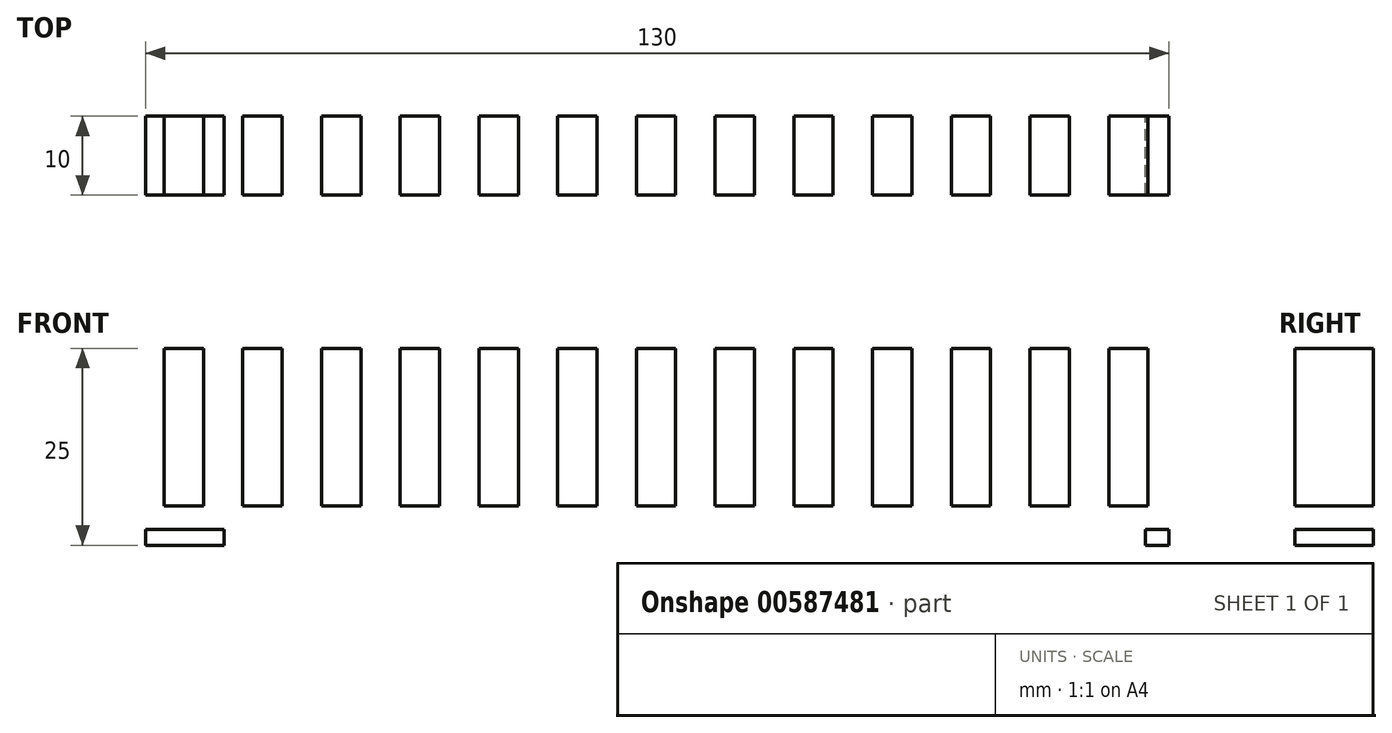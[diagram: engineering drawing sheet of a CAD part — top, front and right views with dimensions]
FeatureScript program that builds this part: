
annotation { "Feature Type Name" : "Feature", "Feature Type Description" : "" }
export const myFeature = defineFeature(function(context is Context, id is Id, definition is map)
    precondition{}
    {
        {
            var Q0;
            Q0=qCreatedBy(makeId("Front.planeOp"),FACE);
            var sketch = newSketch(context, id + "F0", { "sketchPlane" : qUnion([Q0])});
            skLineSegment(sketch, "E0.bottom", {"start": v(-65, 2.5) * mm, "end": v(65, 2.5) * mm});
            skLineSegment(sketch, "E0.top", {"start": v(-65, -2.5) * mm, "end": v(65, -2.5) * mm});
            skLineSegment(sketch, "E0.left", {"start": v(-65, 2.5) * mm, "end": v(-65, -2.5) * mm});
            skLineSegment(sketch, "E0.right", {"start": v(65, 2.5) * mm, "end": v(65, -2.5) * mm});
            skPoint(sketch, "E0.middle", {"position": v(0, 0) * mm});
            skLineSegment(sketch, "E1.bottom", {"start": v(-64.85, 2.5) * mm, "end": v(-59.85, 2.5) * mm});
            skLineSegment(sketch, "E1.top", {"start": v(-62.65, 22.5) * mm, "end": v(-57.65, 22.5) * mm});
            skLineSegment(sketch, "E1.left", {"start": v(-62.65, 2.5) * mm, "end": v(-62.65, 22.5) * mm});
            skLineSegment(sketch, "E1.right", {"start": v(-57.65, 2.5) * mm, "end": v(-57.65, 22.5) * mm});
            skLineSegment(sketch, "E2.1.0.0", {"start": v(-52.65, 22.5) * mm, "end": v(-47.65, 22.5) * mm});
            skLineSegment(sketch, "E2.1.0.1", {"start": v(-47.65, 2.5) * mm, "end": v(-47.65, 22.5) * mm});
            skLineSegment(sketch, "E2.1.0.2", {"start": v(-52.65, 2.5) * mm, "end": v(-52.65, 22.5) * mm});
            skLineSegment(sketch, "E2.2.0.0", {"start": v(-42.65, 22.5) * mm, "end": v(-37.65, 22.5) * mm});
            skLineSegment(sketch, "E2.2.0.1", {"start": v(-37.65, 2.5) * mm, "end": v(-37.65, 22.5) * mm});
            skLineSegment(sketch, "E2.2.0.2", {"start": v(-42.65, 2.5) * mm, "end": v(-42.65, 22.5) * mm});
            skLineSegment(sketch, "E2.3.0.0", {"start": v(-32.65, 22.5) * mm, "end": v(-27.65, 22.5) * mm});
            skLineSegment(sketch, "E2.3.0.1", {"start": v(-27.65, 2.5) * mm, "end": v(-27.65, 22.5) * mm});
            skLineSegment(sketch, "E2.3.0.2", {"start": v(-32.65, 2.5) * mm, "end": v(-32.65, 22.5) * mm});
            skLineSegment(sketch, "E2.4.0.0", {"start": v(-22.65, 22.5) * mm, "end": v(-17.65, 22.5) * mm});
            skLineSegment(sketch, "E2.4.0.1", {"start": v(-17.65, 2.5) * mm, "end": v(-17.65, 22.5) * mm});
            skLineSegment(sketch, "E2.4.0.2", {"start": v(-22.65, 2.5) * mm, "end": v(-22.65, 22.5) * mm});
            skLineSegment(sketch, "E2.5.0.0", {"start": v(-12.65, 22.5) * mm, "end": v(-7.65, 22.5) * mm});
            skLineSegment(sketch, "E2.5.0.1", {"start": v(-7.65, 2.5) * mm, "end": v(-7.65, 22.5) * mm});
            skLineSegment(sketch, "E2.5.0.2", {"start": v(-12.65, 2.5) * mm, "end": v(-12.65, 22.5) * mm});
            skLineSegment(sketch, "E2.6.0.0", {"start": v(-2.65, 22.5) * mm, "end": v(2.35, 22.5) * mm});
            skLineSegment(sketch, "E2.6.0.1", {"start": v(2.35, 2.5) * mm, "end": v(2.35, 22.5) * mm});
            skLineSegment(sketch, "E2.6.0.2", {"start": v(-2.65, 2.5) * mm, "end": v(-2.65, 22.5) * mm});
            skLineSegment(sketch, "E2.7.0.0", {"start": v(7.35, 22.5) * mm, "end": v(12.35, 22.5) * mm});
            skLineSegment(sketch, "E2.7.0.1", {"start": v(12.35, 2.5) * mm, "end": v(12.35, 22.5) * mm});
            skLineSegment(sketch, "E2.7.0.2", {"start": v(7.35, 2.5) * mm, "end": v(7.35, 22.5) * mm});
            skLineSegment(sketch, "E2.8.0.0", {"start": v(17.35, 22.5) * mm, "end": v(22.35, 22.5) * mm});
            skLineSegment(sketch, "E2.8.0.1", {"start": v(22.35, 2.5) * mm, "end": v(22.35, 22.5) * mm});
            skLineSegment(sketch, "E2.8.0.2", {"start": v(17.35, 2.5) * mm, "end": v(17.35, 22.5) * mm});
            skLineSegment(sketch, "E2.9.0.0", {"start": v(27.35, 22.5) * mm, "end": v(32.35, 22.5) * mm});
            skLineSegment(sketch, "E2.9.0.1", {"start": v(32.35, 2.5) * mm, "end": v(32.35, 22.5) * mm});
            skLineSegment(sketch, "E2.9.0.2", {"start": v(27.35, 2.5) * mm, "end": v(27.35, 22.5) * mm});
            skLineSegment(sketch, "E3.1.0.0", {"start": v(37.35, 2.5) * mm, "end": v(37.35, 22.5) * mm});
            skLineSegment(sketch, "E3.1.0.1", {"start": v(37.35, 22.5) * mm, "end": v(42.35, 22.5) * mm});
            skLineSegment(sketch, "E3.1.0.2", {"start": v(42.35, 2.5) * mm, "end": v(42.35, 22.5) * mm});
            skLineSegment(sketch, "E3.2.0.0", {"start": v(47.35, 2.5) * mm, "end": v(47.35, 22.5) * mm});
            skLineSegment(sketch, "E3.2.0.1", {"start": v(47.35, 22.5) * mm, "end": v(52.35, 22.5) * mm});
            skLineSegment(sketch, "E3.2.0.2", {"start": v(52.35, 2.5) * mm, "end": v(52.35, 22.5) * mm});
            skLineSegment(sketch, "E3.3.0.0", {"start": v(57.35, 2.5) * mm, "end": v(57.35, 22.5) * mm});
            skLineSegment(sketch, "E3.3.0.1", {"start": v(57.35, 22.5) * mm, "end": v(62.35, 22.5) * mm});
            skLineSegment(sketch, "E3.3.0.2", {"start": v(62.35, 2.5) * mm, "end": v(62.35, 22.5) * mm});
            skLineSegment(sketch, "E3.direction1", {"start": v(25.15, 2.5) * mm, "end": v(35.15, 2.5) * mm, "construction": true});
            skLineSegment(sketch, "E4.bottom", {"start": v(65, -0.5) * mm, "end": v(62, -0.5) * mm});
            skLineSegment(sketch, "E4.top", {"start": v(65, -2.5) * mm, "end": v(62, -2.5) * mm});
            skLineSegment(sketch, "E4.left", {"start": v(65, -0.5) * mm, "end": v(65, -2.5) * mm});
            skLineSegment(sketch, "E4.right", {"start": v(62, -0.5) * mm, "end": v(62, -2.5) * mm});
            skLineSegment(sketch, "E5.bottom", {"start": v(-65, -0.5) * mm, "end": v(-55, -0.5) * mm});
            skLineSegment(sketch, "E5.top", {"start": v(-65, -2.5) * mm, "end": v(-55, -2.5) * mm});
            skLineSegment(sketch, "E5.left", {"start": v(-65, -0.5) * mm, "end": v(-65, -2.5) * mm});
            skLineSegment(sketch, "E5.right", {"start": v(-55, -0.5) * mm, "end": v(-55, -2.5) * mm});
            skSolve(sketch);
        }
        {
            var Q0;
            {var subQ0=sQuery(id+"F0.wireOp",EDGE,"E3.3.0.0");Q0=makeQuery(id+"F0.imprint","IMPRINT",FACE,{"disambiguationData":[TD([[makeQuery(id+"F0.imprint","IMPRINT",EDGE,{"derivedFrom":subQ0}),-1.0]])]});}
            var Q1;
            {var subQ0=sQuery(id+"F0.wireOp",EDGE,"E3.2.0.0");Q1=makeQuery(id+"F0.imprint","IMPRINT",FACE,{"disambiguationData":[TD([[makeQuery(id+"F0.imprint","IMPRINT",EDGE,{"derivedFrom":subQ0}),-1.0]])]});}
            var Q2;
            {var subQ0=sQuery(id+"F0.wireOp",EDGE,"E3.1.0.0");Q2=makeQuery(id+"F0.imprint","IMPRINT",FACE,{"disambiguationData":[TD([[makeQuery(id+"F0.imprint","IMPRINT",EDGE,{"derivedFrom":subQ0}),-1.0]])]});}
            var Q3;
            Q3=makeQuery(id+"F0.imprint","IMPRINT",FACE,{"disambiguationData":[TD([[makeQuery(id+"F0.imprint","IMPRINT",EDGE,{"derivedFrom":sQuery(id+"F0.wireOp",EDGE,"E2.9.0.0")}),-1.0]])]});
            var Q4;
            Q4=makeQuery(id+"F0.imprint","IMPRINT",FACE,{"disambiguationData":[TD([[makeQuery(id+"F0.imprint","IMPRINT",EDGE,{"derivedFrom":sQuery(id+"F0.wireOp",EDGE,"E2.8.0.0")}),-1.0]])]});
            var Q5;
            Q5=makeQuery(id+"F0.imprint","IMPRINT",FACE,{"disambiguationData":[TD([[makeQuery(id+"F0.imprint","IMPRINT",EDGE,{"derivedFrom":sQuery(id+"F0.wireOp",EDGE,"E2.7.0.0")}),-1.0]])]});
            var Q6;
            Q6=makeQuery(id+"F0.imprint","IMPRINT",FACE,{"disambiguationData":[TD([[makeQuery(id+"F0.imprint","IMPRINT",EDGE,{"derivedFrom":sQuery(id+"F0.wireOp",EDGE,"E2.6.0.0")}),-1.0]])]});
            var Q7;
            Q7=makeQuery(id+"F0.imprint","IMPRINT",FACE,{"disambiguationData":[TD([[makeQuery(id+"F0.imprint","IMPRINT",EDGE,{"derivedFrom":sQuery(id+"F0.wireOp",EDGE,"E2.5.0.0")}),-1.0]])]});
            var Q8;
            Q8=makeQuery(id+"F0.imprint","IMPRINT",FACE,{"disambiguationData":[TD([[makeQuery(id+"F0.imprint","IMPRINT",EDGE,{"derivedFrom":sQuery(id+"F0.wireOp",EDGE,"E2.4.0.0")}),-1.0]])]});
            var Q9;
            Q9=makeQuery(id+"F0.imprint","IMPRINT",FACE,{"disambiguationData":[TD([[makeQuery(id+"F0.imprint","IMPRINT",EDGE,{"derivedFrom":sQuery(id+"F0.wireOp",EDGE,"E2.3.0.0")}),-1.0]])]});
            var Q10;
            Q10=makeQuery(id+"F0.imprint","IMPRINT",FACE,{"disambiguationData":[TD([[makeQuery(id+"F0.imprint","IMPRINT",EDGE,{"derivedFrom":sQuery(id+"F0.wireOp",EDGE,"E2.2.0.0")}),-1.0]])]});
            var Q11;
            Q11=makeQuery(id+"F0.imprint","IMPRINT",FACE,{"disambiguationData":[TD([[makeQuery(id+"F0.imprint","IMPRINT",EDGE,{"derivedFrom":sQuery(id+"F0.wireOp",EDGE,"E2.1.0.0")}),-1.0]])]});
            var Q12;
            Q12=makeQuery(id+"F0.imprint","IMPRINT",FACE,{"disambiguationData":[TD([[makeQuery(id+"F0.imprint","IMPRINT",EDGE,{"derivedFrom":sQuery(id+"F0.wireOp",EDGE,"E1.top")}),-1.0]])]});
            var Q13;
            Q13=makeQuery(id+"F0.imprint","IMPRINT",FACE,{"disambiguationData":[TD([[makeQuery(id+"F0.imprint","IMPRINT",EDGE,{"derivedFrom":sQuery(id+"F0.wireOp",EDGE,"E0.top")}),1.0]])]});
            extrude(context, id + "F1", {"entities" : qUnion([Q0, Q1, Q2, Q3, Q4, Q5, Q6, Q7, Q8, Q9, Q10, Q11, Q12, Q13]), "depth" : 10 * mm, "offsetDistance" : 25 * mm});
        }
    });
